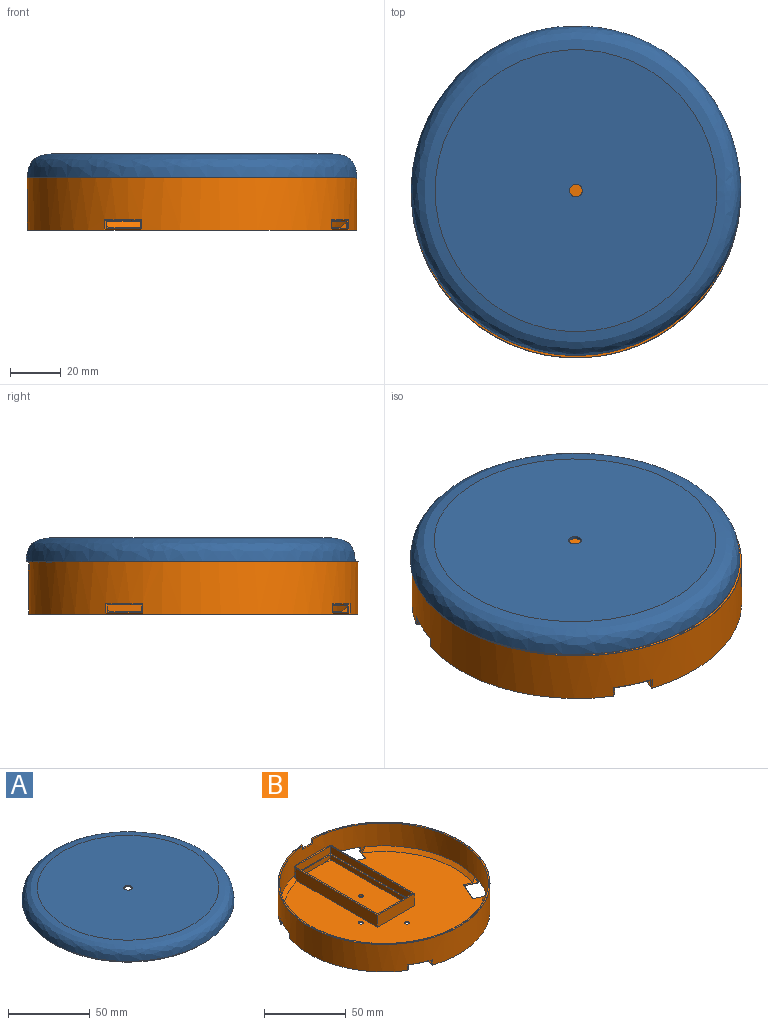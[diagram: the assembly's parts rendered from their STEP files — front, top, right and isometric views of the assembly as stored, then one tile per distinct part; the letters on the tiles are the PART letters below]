
ASSEMBLY  parts=2 mates=1
PART A: 18 faces, bbox 132x132x13 mm
  f0: offset ~132x132mm, area 1027.2mm2, adj f3,f4,f14,f15,f16
  f1: plane 111.19x111.19mm, normal (0,0,1), area 9685.4mm2, adj f2,f17
  f2: bspline ~130x130mm, area 5864.8mm2, adj f1,f3,f14,f15,f16
  f3: plane 130.18x130.15mm, normal (0,0,-1), area 398.4mm2, adj f0,f2,f15,f16
  f4: cylinder r=63.75mm len=127.5mm, axis (0,0,-1), area 1137.5mm2, adj f0,f10,f11,f12,f13
  f5: plane 126.48x126.47mm, normal (0,0,1), area 216.7mm2, adj f6,f9
  f6: cylinder r=62.68mm len=125.36mm, axis (0,0,-1), area 2326.9mm2, adj f5,f7,f11,f12,f13
  f7: plane 126.75x126.71mm, normal (0,0,-1), area 269.4mm2, adj f6,f10,f11,f12
  f8: plane 111.17x111.17mm, normal (0,0,-1), area 9685.4mm2, adj f9,f17
  f9: offset ~132x132mm, area 3459.7mm2, adj f5,f8
  f10: cone r=63.75mm half-angle=15deg, axis (0,0,1), area 565.8mm2, adj f4,f7,f11,f12
  f11: plane 4x1.07mm, normal (-1,0,0), area 4mm2, adj f4,f6,f7,f10,f13
  f12: plane 4x1.08mm, normal (1,0,0), area 4mm2, adj f4,f6,f7,f10,f13
  f13: plane 9x1.44mm, normal (0,0,-1), area 9.7mm2, adj f4,f6,f11,f12
  f14: plane 9x1.38mm, normal (0,0,-1), area 9.1mm2, adj f0,f2,f15,f16
  f15: plane 2.4x1.3mm, normal (1,0,0), area 2.3mm2, adj f0,f2,f3,f14
  f16: plane 2.4x1.29mm, normal (-1,0,0), area 2.3mm2, adj f0,f2,f3,f14
  f17: cylinder r=2.5mm len=5mm, axis (0,0,1), area 15.7mm2, adj f1,f8
PART B: 89 faces, bbox 175.3x175.3x66 mm
  f0: plane 30.5x5.5mm, normal (0,1,0), area 167.7mm2, adj f1,f86,f87,f88
  f1: plane 73.5x32.5mm, normal (0,0,1), area 203mm2, adj f0,f2,f78,f79,f80,f81,f83,f84
  f2: plane 71.18x9.29mm, normal (1,0,0), area 639.9mm2, adj f1,f3,f4,f5,f76,f77,f78,f84
  f3: cone r=61.5mm half-angle=45deg, axis (0,0,1), area 6.3mm2, adj f2,f4,f5,f83,f84
  f4: plane 5.54x2.27mm, normal (0,0,1), area 6.3mm2, adj f2,f3,f5
  f5: plane 8.6x4.04mm, normal (0.64,-0.3,0.71), area 10.5mm2, adj f2,f3,f4,f6,f75,f76,f83
  f6: plane 3.1x0.61mm, normal (0.4,-0.92,0), area 1.9mm2, adj f5,f7,f74,f83
  f7: plane 14.28x6.81mm, normal (0,0,-1), area 7.6mm2, adj f6,f8,f72,f73,f74,f83
  f8: plane 3.1x0.4mm, normal (-0.91,0.42,0), area 1.4mm2, adj f7,f9,f72,f83
  f9: plane 8.83x4.36mm, normal (-0.64,0.3,-0.71), area 6.6mm2, adj f8,f10,f58,f60,f72
  f10: plane 8.28x6.11mm, normal (-0.64,0.3,0.71), area 10.5mm2, adj f9,f11,f76,f77,f83
  f11: cone r=61.5mm half-angle=45deg, axis (0,0,1), area 282.9mm2, adj f10,f12,f77,f83
  f12: plane 8.74x4.42mm, normal (-0.3,-0.64,0.71), area 10.7mm2, adj f11,f13,f56,f57,f77,f83
  f13: plane 3.1x0.61mm, normal (-0.92,-0.4,0), area 1.9mm2, adj f12,f14,f55,f83
  f14: plane 14.39x7.05mm, normal (0,0,-1), area 7.7mm2, adj f13,f15,f53,f54,f55,f83
  f15: plane 3.1x0.63mm, normal (-0.28,0.96,0), area 1.9mm2, adj f14,f16,f53,f83
  f16: plane 8.68x6.11mm, normal (0.3,0.64,0.71), area 10.7mm2, adj f15,f17,f51,f57,f77,f83
  f17: cone r=61.5mm half-angle=45deg, axis (0,0,1), area 282.9mm2, adj f16,f18,f77,f83
  f18: plane 8.74x4.42mm, normal (-0.64,0.3,0.71), area 10.7mm2, adj f17,f19,f49,f50,f77,f83
  f19: plane 3.1x0.61mm, normal (-0.4,0.92,0), area 1.9mm2, adj f18,f20,f48,f83
  f20: plane 14.39x7.05mm, normal (0,0,-1), area 7.7mm2, adj f19,f21,f46,f47,f48,f83
  f21: plane 3.1x0.63mm, normal (0.96,0.28,0), area 1.9mm2, adj f20,f22,f46,f83
  f22: plane 8.68x6.11mm, normal (0.64,-0.3,0.71), area 10.7mm2, adj f21,f23,f25,f50,f77,f83
  f23: plane 8.83x4.36mm, normal (0.64,-0.3,-0.71), area 6.6mm2, adj f22,f24,f46,f60
  f24: plane 14.5x7mm, normal (-0.3,-0.64,-0.71), area 11mm2, adj f23,f49,f50,f60
  f25: cone r=61.5mm half-angle=45deg, axis (0,0,1), area 282.9mm2, adj f22,f26,f77,f83
  f26: plane 8.74x4.42mm, normal (0.3,0.64,0.71), area 10.7mm2, adj f25,f27,f44,f45,f77,f83
  f27: plane 3.1x0.61mm, normal (0.92,0.4,0), area 1.9mm2, adj f26,f28,f43,f83
  f28: plane 14.39x7.05mm, normal (0,0,-1), area 7.7mm2, adj f27,f29,f34,f42,f43,f83
  f29: plane 3.1x0.63mm, normal (0.28,-0.96,0), area 1.9mm2, adj f28,f30,f34,f83
  f30: plane 8.68x6.11mm, normal (-0.3,-0.64,0.71), area 10.7mm2, adj f29,f31,f32,f45,f77,f83
  f31: cone r=61.5mm half-angle=45deg, axis (0,0,1), area 161.2mm2, adj f30,f77,f79,f80,f83
  f32: plane 8.83x4.36mm, normal (-0.3,-0.64,-0.71), area 6.6mm2, adj f30,f33,f34,f60
  f33: plane 14.5x7mm, normal (-0.64,0.3,-0.71), area 11mm2, adj f32,f44,f45,f60
  f34: plane 4.1x0.72mm, normal (-0.96,-0.28,0), area 2.7mm2, adj f28,f29,f32,f35,f42,f60
  f35: cylinder r=65mm len=130mm, axis (0,0,-1), area 8114mm2, adj f34,f36,f39,f40,f41,f42,f43,f46
  f36: plane 48.49x46.29mm, normal (-1,0,0), area 3.2mm2, adj f35,f37,f38,f39,f41,f83
  f37: plane 175.3x175.27mm, normal (0,0,1), area 393.4mm2, adj f36,f38,f40,f41
  f38: offset ~131.92x131.61mm, area 47.7mm2, adj f36,f37,f40,f83
  f39: plane 9x1.36mm, normal (0,0,1), area 9mm2, adj f35,f36,f40,f83
  f40: plane 3.2x1.01mm, normal (1,0,0), area 3.2mm2, adj f35,f37,f38,f39,f41,f83
  f41: bspline ~129.94x129.92mm, area 46.1mm2, adj f35,f36,f37,f40
  f42: cone r=64.5mm half-angle=45deg, axis (0,0,1), area 11.1mm2, adj f28,f34,f35,f43
  f43: plane 4.1x0.69mm, normal (-0.4,0.92,0), area 2.7mm2, adj f27,f28,f35,f42,f44,f60
  f44: plane 8.83x4.39mm, normal (0.3,0.64,-0.71), area 6.6mm2, adj f26,f33,f43,f60
  f45: plane 14.5x7mm, normal (-0.64,0.3,0.71), area 11mm2, adj f26,f30,f33,f77
  f46: plane 4.1x0.72mm, normal (0.28,-0.96,0), area 2.7mm2, adj f20,f21,f23,f35,f47,f60
  f47: cone r=64.5mm half-angle=45deg, axis (0,0,1), area 11.1mm2, adj f20,f35,f46,f48
  f48: plane 4.1x0.69mm, normal (-0.92,-0.4,0), area 2.7mm2, adj f19,f20,f35,f47,f49,f60
  f49: plane 8.83x4.39mm, normal (-0.64,0.3,-0.71), area 6.6mm2, adj f18,f24,f48,f60
  f50: plane 14.5x7mm, normal (-0.3,-0.64,0.71), area 11mm2, adj f18,f22,f24,f77
  f51: plane 8.83x4.36mm, normal (0.3,0.64,-0.71), area 6.6mm2, adj f16,f52,f53,f60
  f52: plane 14.5x7mm, normal (0.64,-0.3,-0.71), area 11mm2, adj f51,f56,f57,f60
  f53: plane 4.1x0.72mm, normal (0.96,0.28,0), area 2.7mm2, adj f14,f15,f35,f51,f54,f60
  f54: cone r=64.5mm half-angle=45deg, axis (0,0,1), area 11.1mm2, adj f14,f35,f53,f55
  f55: plane 4.1x0.69mm, normal (0.4,-0.92,0), area 2.7mm2, adj f13,f14,f35,f54,f56,f60
  f56: plane 8.83x4.39mm, normal (-0.3,-0.64,-0.71), area 6.6mm2, adj f12,f52,f55,f60
  f57: plane 14.5x7mm, normal (0.64,-0.3,0.71), area 11mm2, adj f12,f16,f52,f77
  f58: plane 14.12x7mm, normal (0.3,0.64,-0.71), area 10.9mm2, adj f9,f59,f60,f75,f76
  f59: plane 1x0.29mm, normal (1,0,0), area 0.1mm2, adj f58,f60,f75
  f60: plane 130x130mm, normal (0,0,-1), area 12596.2mm2, adj f9,f23,f24,f32,f33,f34,f35,f43
  f61: cylinder r=1.5mm len=3mm, axis (0,0,-1), area 9.4mm2, adj f60,f77
  f62: cylinder r=1.5mm len=3mm, axis (0,0,-1), area 9.4mm2, adj f60,f77
  f63: cylinder r=1.5mm len=3mm, axis (0,0,-1), area 9.4mm2, adj f60,f77
  f64: cylinder r=1.5mm len=3mm, axis (0,0,-1), area 9.4mm2, adj f60,f65
  f65: plane 69.5x28.5mm, normal (0,0,1), area 1967.4mm2, adj f64,f66,f67,f68,f69,f70,f71
  f66: plane 69.5x3.5mm, normal (-1,0,0), area 242.6mm2, adj f65,f67,f70,f71,f87
  f67: plane 28.5x3.5mm, normal (0,1,0), area 99.7mm2, adj f65,f66,f68,f87
  f68: plane 69.5x3.5mm, normal (1,0,0), area 242.6mm2, adj f65,f67,f69,f70,f87
  f69: cone r=61.5mm half-angle=45deg, axis (0,0,1), area 4.8mm2, adj f65,f68,f70
  f70: plane 28.71x3.72mm, normal (0,-1,0), area 93.6mm2, adj f65,f66,f68,f69,f71,f87
  f71: cone r=61.5mm half-angle=45deg, axis (0,0,1), area 4.8mm2, adj f65,f66,f70
  f72: plane 4.1x0.72mm, normal (-0.28,0.96,0), area 2.7mm2, adj f7,f8,f9,f35,f60,f73
  f73: cone r=64.5mm half-angle=45deg, axis (0,0,1), area 11.1mm2, adj f7,f35,f72,f74
  f74: plane 4.1x0.69mm, normal (0.92,0.4,0), area 2.7mm2, adj f6,f7,f35,f60,f73,f75
  f75: plane 8.69x4mm, normal (0.64,-0.3,-0.71), area 6.4mm2, adj f5,f58,f59,f60,f74
  f76: plane 14.12x7mm, normal (0.3,0.64,0.71), area 10.9mm2, adj f2,f5,f10,f58,f77
  f77: plane 123x120.81mm, normal (0,0,1), area 9112.8mm2, adj f2,f10,f11,f12,f16,f17,f18,f22
  f78: plane 32.5x9mm, normal (0,-1,0), area 292.5mm2, adj f1,f2,f77,f79
  f79: plane 71.18x9mm, normal (-1,0,0), area 639.7mm2, adj f1,f31,f77,f78,f80
  f80: cylinder r=2.33mm len=7.73mm, axis (0,0,-1), area 10.6mm2, adj f1,f31,f79,f83
  f81: plane 26x10.51mm, normal (0,1,0), area 165.6mm2, adj f1,f82,f83
  f82: cone r=61.5mm half-angle=45deg, axis (0,0,1), area 0mm2, adj f81,f83
  f83: cylinder r=64mm len=128mm, axis (0,0,-1), area 6806.8mm2, adj f1,f3,f5,f6,f7,f8,f10,f11
  f84: cylinder r=2.33mm len=7.73mm, axis (0,0,-1), area 10.6mm2, adj f1,f2,f3,f83
  f85: plane 30.5x5.5mm, normal (0,-1,0), area 167.7mm2, adj f1,f86,f87,f88
  f86: plane 71.5x5.5mm, normal (1,0,0), area 393.3mm2, adj f0,f1,f85,f87
  f87: plane 71.5x30.5mm, normal (0,0,1), area 200mm2, adj f0,f66,f67,f68,f70,f85,f86,f88
  f88: plane 71.5x5.5mm, normal (-1,0,0), area 393.3mm2, adj f0,f1,f85,f87
PLACE A t=(-1,1.99,0)mm
PLACE B t=(-1,0.99,0)mm
MATE slider A.f3 <-> B.f37  axis (0,0,1) through (1.24,-62.97,20.7)mm
